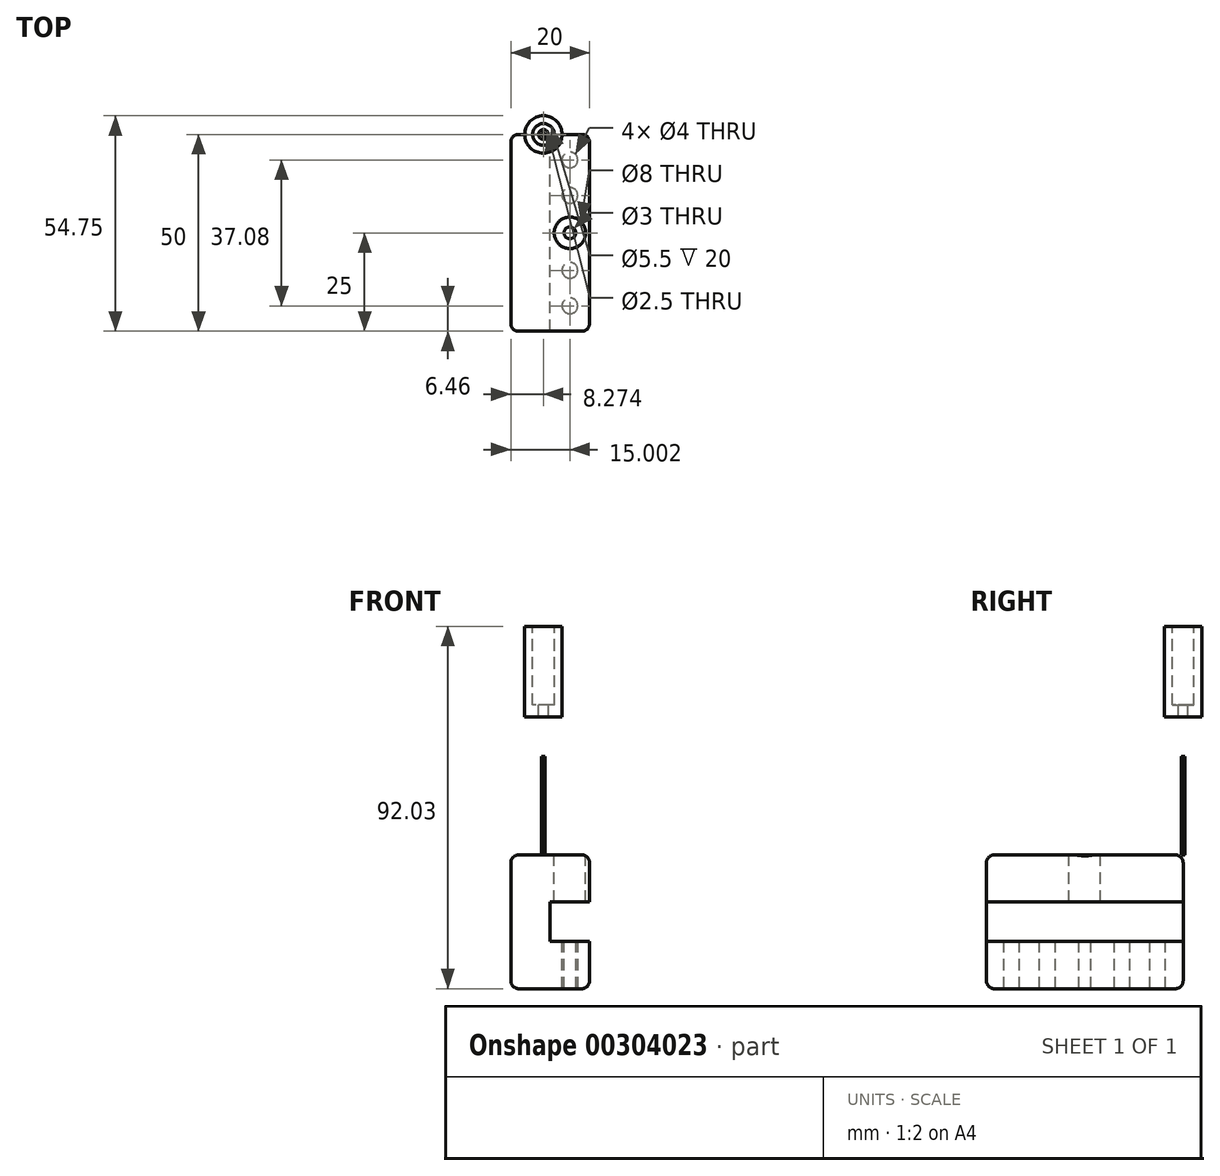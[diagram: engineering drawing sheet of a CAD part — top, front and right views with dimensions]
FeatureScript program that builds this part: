
annotation { "Feature Type Name" : "Feature", "Feature Type Description" : "" }
export const myFeature = defineFeature(function(context is Context, id is Id, definition is map)
    precondition{}
    {
        {
            var Q0;
            Q0=qCreatedBy(makeId("Front.planeOp"),FACE);
            var sketch = newSketch(context, id + "F0", { "sketchPlane" : qUnion([Q0])});
            skLineSegment(sketch, "E0", {"start": v(1.64, 12) * mm, "end": v(21.64, 12) * mm});
            skLineSegment(sketch, "E1", {"start": v(21.64, 12) * mm, "end": v(21.64, 0) * mm});
            skLineSegment(sketch, "E2", {"start": v(21.64, 0) * mm, "end": v(11.64, 0) * mm});
            skLineSegment(sketch, "E3", {"start": v(11.64, 0) * mm, "end": v(11.64, -10) * mm});
            skLineSegment(sketch, "E4", {"start": v(11.64, -10) * mm, "end": v(21.64, -10) * mm});
            skLineSegment(sketch, "E5", {"start": v(21.64, -10) * mm, "end": v(21.64, -22) * mm});
            skLineSegment(sketch, "E6", {"start": v(21.64, -22) * mm, "end": v(1.64, -22) * mm});
            skLineSegment(sketch, "E7", {"start": v(1.64, -22) * mm, "end": v(1.64, 12) * mm});
            skSolve(sketch);
        }
        {
            var Q0;
            Q0=makeQuery(id+"F0.imprint","IMPRINT",FACE,{"disambiguationData":[TD([[makeQuery(id+"F0.imprint","IMPRINT",EDGE,{"derivedFrom":sQuery(id+"F0.wireOp",EDGE,"E0")}),-1.0]])]});
            extrude(context, id + "F1", {"entities" : qUnion([Q0]), "depth" : 50 * mm});
        }
        {
            var Q0;
            Q0=makeQuery(id+"F1.opExtrude","SWEPT_FACE",FACE,{"disambiguationData":[OSD([sQuery(id+"F0.wireOp",EDGE,"E0")])]});
            var sketch = newSketch(context, id + "F2", { "sketchPlane" : qUnion([Q0])});
            skPoint(sketch, "E8", {"position": v(16.64, -25) * mm});
            skSolve(sketch);
        }
        {
            var Q0;
            Q0=sQuery(id+"F2.wireOp",VERTEX,"E8");
            var Q1;
            Q1=makeQuery(id+"F1.opExtrude","SWEPT_BODY",BODY,{"disambiguationData":[OSD([sQuery(id+"F0.wireOp",EDGE,"E0"),sQuery(id+"F0.wireOp",EDGE,"E1"),sQuery(id+"F0.wireOp",EDGE,"E2"),sQuery(id+"F0.wireOp",EDGE,"E3"),sQuery(id+"F0.wireOp",EDGE,"E4"),sQuery(id+"F0.wireOp",EDGE,"E5"),sQuery(id+"F0.wireOp",EDGE,"E6"),sQuery(id+"F0.wireOp",EDGE,"E7")])]});
            hole(context, id + "F3", {"style" : HoleStyle.SIMPLE, "endStyle" : HoleEndStyle.BLIND, "holeDiameter" : 8 * mm, "holeDepth" : 12 * mm, "tappedDepth" : 12 * mm, "tapClearance" : 3, "locations" : qUnion([Q0]), "scope" : qUnion([Q1])});
        }
        {
            var Q0;
            Q0=makeQuery(id+"F1.opExtrude","SWEPT_FACE",FACE,{"disambiguationData":[OSD([sQuery(id+"F0.wireOp",EDGE,"E4")])]});
            var sketch = newSketch(context, id + "F4", { "sketchPlane" : qUnion([Q0])});
            skPoint(sketch, "E9", {"position": v(16.64, -25) * mm});
            skSolve(sketch);
        }
        {
            var Q0;
            Q0=sQuery(id+"F4.wireOp",VERTEX,"E9");
            var Q1;
            Q1=makeQuery(id+"F1.opExtrude","SWEPT_BODY",BODY,{"disambiguationData":[OSD([sQuery(id+"F0.wireOp",EDGE,"E0"),sQuery(id+"F0.wireOp",EDGE,"E1"),sQuery(id+"F0.wireOp",EDGE,"E2"),sQuery(id+"F0.wireOp",EDGE,"E3"),sQuery(id+"F0.wireOp",EDGE,"E4"),sQuery(id+"F0.wireOp",EDGE,"E5"),sQuery(id+"F0.wireOp",EDGE,"E6"),sQuery(id+"F0.wireOp",EDGE,"E7")])]});
            hole(context, id + "F5", {"style" : HoleStyle.SIMPLE, "endStyle" : HoleEndStyle.THROUGH, "holeDiameter" : 3 * mm, "tappedDepth" : 12 * mm, "tapClearance" : 3, "locations" : qUnion([Q0]), "scope" : qUnion([Q1])});
        }
        {
            var Q0;
            Q0=makeQuery(id+"F1.opExtrude","SWEPT_FACE",FACE,{"disambiguationData":[OSD([sQuery(id+"F0.wireOp",EDGE,"E4")])]});
            var sketch = newSketch(context, id + "F6", { "sketchPlane" : qUnion([Q0])});
            skPoint(sketch, "E10", {"position": v(16.64, -34.52) * mm});
            skSolve(sketch);
        }
        {
            var Q0;
            Q0=sQuery(id+"F6.wireOp",VERTEX,"E10");
            var Q1;
            Q1=makeQuery(id+"F1.opExtrude","SWEPT_BODY",BODY,{"disambiguationData":[OSD([sQuery(id+"F0.wireOp",EDGE,"E0"),sQuery(id+"F0.wireOp",EDGE,"E1"),sQuery(id+"F0.wireOp",EDGE,"E2"),sQuery(id+"F0.wireOp",EDGE,"E3"),sQuery(id+"F0.wireOp",EDGE,"E4"),sQuery(id+"F0.wireOp",EDGE,"E5"),sQuery(id+"F0.wireOp",EDGE,"E6"),sQuery(id+"F0.wireOp",EDGE,"E7")])]});
            hole(context, id + "F7", {"style" : HoleStyle.SIMPLE, "endStyle" : HoleEndStyle.THROUGH, "holeDiameter" : 4 * mm, "tappedDepth" : 12 * mm, "tapClearance" : 3, "locations" : qUnion([Q0]), "scope" : qUnion([Q1])});
        }
        {
            var Q0;
            Q0=makeQuery(id+"F1.opExtrude","SWEPT_FACE",FACE,{"disambiguationData":[OSD([sQuery(id+"F0.wireOp",EDGE,"E4")])]});
            var sketch = newSketch(context, id + "F8", { "sketchPlane" : qUnion([Q0])});
            skPoint(sketch, "E11", {"position": v(16.64, -15.48) * mm});
            skSolve(sketch);
        }
        {
            var Q0;
            Q0=sQuery(id+"F8.wireOp",VERTEX,"E11");
            var Q1;
            Q1=makeQuery(id+"F1.opExtrude","SWEPT_BODY",BODY,{"disambiguationData":[OSD([sQuery(id+"F0.wireOp",EDGE,"E0"),sQuery(id+"F0.wireOp",EDGE,"E1"),sQuery(id+"F0.wireOp",EDGE,"E2"),sQuery(id+"F0.wireOp",EDGE,"E3"),sQuery(id+"F0.wireOp",EDGE,"E4"),sQuery(id+"F0.wireOp",EDGE,"E5"),sQuery(id+"F0.wireOp",EDGE,"E6"),sQuery(id+"F0.wireOp",EDGE,"E7")])]});
            hole(context, id + "F9", {"style" : HoleStyle.SIMPLE, "endStyle" : HoleEndStyle.THROUGH, "holeDiameter" : 4 * mm, "tappedDepth" : 12 * mm, "tapClearance" : 3, "locations" : qUnion([Q0]), "scope" : qUnion([Q1])});
        }
        {
            var Q0;
            Q0=makeQuery(id+"F1.opExtrude","SWEPT_FACE",FACE,{"disambiguationData":[OSD([sQuery(id+"F0.wireOp",EDGE,"E4")])]});
            var sketch = newSketch(context, id + "F10", { "sketchPlane" : qUnion([Q0])});
            skPoint(sketch, "E12", {"position": v(16.64, -6.46) * mm});
            skSolve(sketch);
        }
        {
            var Q0;
            Q0=sQuery(id+"F10.wireOp",VERTEX,"E12");
            var Q1;
            Q1=makeQuery(id+"F1.opExtrude","SWEPT_BODY",BODY,{"disambiguationData":[OSD([sQuery(id+"F0.wireOp",EDGE,"E0"),sQuery(id+"F0.wireOp",EDGE,"E1"),sQuery(id+"F0.wireOp",EDGE,"E2"),sQuery(id+"F0.wireOp",EDGE,"E3"),sQuery(id+"F0.wireOp",EDGE,"E4"),sQuery(id+"F0.wireOp",EDGE,"E5"),sQuery(id+"F0.wireOp",EDGE,"E6"),sQuery(id+"F0.wireOp",EDGE,"E7")])]});
            hole(context, id + "F11", {"style" : HoleStyle.SIMPLE, "endStyle" : HoleEndStyle.THROUGH, "holeDiameter" : 4 * mm, "tappedDepth" : 12 * mm, "tapClearance" : 3, "locations" : qUnion([Q0]), "scope" : qUnion([Q1])});
        }
        {
            var Q0;
            Q0=makeQuery(id+"F1.opExtrude","SWEPT_FACE",FACE,{"disambiguationData":[OSD([sQuery(id+"F0.wireOp",EDGE,"E4")])]});
            var sketch = newSketch(context, id + "F12", { "sketchPlane" : qUnion([Q0])});
            skPoint(sketch, "E13", {"position": v(16.64, -43.54) * mm});
            skSolve(sketch);
        }
        {
            var Q0;
            Q0=sQuery(id+"F12.wireOp",VERTEX,"E13");
            var Q1;
            Q1=makeQuery(id+"F1.opExtrude","SWEPT_BODY",BODY,{"disambiguationData":[OSD([sQuery(id+"F0.wireOp",EDGE,"E0"),sQuery(id+"F0.wireOp",EDGE,"E1"),sQuery(id+"F0.wireOp",EDGE,"E2"),sQuery(id+"F0.wireOp",EDGE,"E3"),sQuery(id+"F0.wireOp",EDGE,"E4"),sQuery(id+"F0.wireOp",EDGE,"E5"),sQuery(id+"F0.wireOp",EDGE,"E6"),sQuery(id+"F0.wireOp",EDGE,"E7")])]});
            hole(context, id + "F13", {"style" : HoleStyle.SIMPLE, "endStyle" : HoleEndStyle.THROUGH, "holeDiameter" : 4 * mm, "tappedDepth" : 12 * mm, "tapClearance" : 3, "locations" : qUnion([Q0]), "scope" : qUnion([Q1])});
        }
        {
            var Q0;
            Q0=makeQuery(id+"F1.opExtrude","SWEPT_EDGE",EDGE,{"disambiguationData":[OSD([sQuery(id+"F0.wireOp",EDGE,"E0"),sQuery(id+"F0.wireOp",EDGE,"E1")])]});
            fillet(context, id + "F14", {"entities" : qUnion([Q0]), "radius" : 2 * mm, "tangentPropagation" : true, "allowEdgeOverflow" : false});
        }
        {
            var Q0;
            Q0=makeQuery(id+"F1.opExtrude","SWEPT_EDGE",EDGE,{"disambiguationData":[OSD([sQuery(id+"F0.wireOp",EDGE,"E5"),sQuery(id+"F0.wireOp",EDGE,"E6")])]});
            fillet(context, id + "F15", {"entities" : qUnion([Q0]), "radius" : 2 * mm, "tangentPropagation" : true, "allowEdgeOverflow" : false});
        }
        {
            var Q0;
            Q0=makeQuery(id+"F1.opExtrude","SWEPT_EDGE",EDGE,{"disambiguationData":[OSD([sQuery(id+"F0.wireOp",EDGE,"E0"),sQuery(id+"F0.wireOp",EDGE,"E7")])]});
            var Q1;
            Q1=makeQuery(id+"F1.opExtrude","SWEPT_EDGE",EDGE,{"disambiguationData":[OSD([sQuery(id+"F0.wireOp",EDGE,"E6"),sQuery(id+"F0.wireOp",EDGE,"E7")])]});
            fillet(context, id + "F16", {"entities" : qUnion([Q0, Q1]), "radius" : 2 * mm, "tangentPropagation" : true, "allowEdgeOverflow" : false});
        }
        {
            var Q0;
            Q0=makeQuery(id+"F1.opExtrude","CAP_EDGE",EDGE,{"disambiguationData":[OSD([sQuery(id+"F0.wireOp",EDGE,"E6")])],"isStart":false});
            var Q1;
            Q1=makeQuery(id+"F1.opExtrude","CAP_EDGE",EDGE,{"disambiguationData":[OSD([sQuery(id+"F0.wireOp",EDGE,"E7")])],"isStart":false});
            var Q2;
            Q2=makeQuery(id+"F1.opExtrude","CAP_EDGE",EDGE,{"disambiguationData":[OSD([sQuery(id+"F0.wireOp",EDGE,"E0")])],"isStart":false});
            var Q3;
            Q3=makeQuery(id+"F1.opExtrude","CAP_EDGE",EDGE,{"disambiguationData":[OSD([sQuery(id+"F0.wireOp",EDGE,"E0")])],"isStart":true});
            var Q4;
            Q4=makeQuery(id+"F1.opExtrude","CAP_EDGE",EDGE,{"disambiguationData":[OSD([sQuery(id+"F0.wireOp",EDGE,"E7")])],"isStart":true});
            fillet(context, id + "F17", {"entities" : qUnion([Q0, Q1, Q2, Q3, Q4]), "radius" : 2 * mm, "tangentPropagation" : true, "allowEdgeOverflow" : false});
        }
        {
            var Q0;
            Q0=qCreatedBy(makeId("Front.planeOp"),FACE);
            var sketch = newSketch(context, id + "F18", { "sketchPlane" : qUnion([Q0])});
            skLineSegment(sketch, "E14", {"start": v(14.66, 47.03) * mm, "end": v(14.66, 70.03) * mm});
            skLineSegment(sketch, "E15", {"start": v(14.66, 70.03) * mm, "end": v(12.66, 70.03) * mm});
            skLineSegment(sketch, "E16", {"start": v(12.66, 70.03) * mm, "end": v(12.66, 50.03) * mm});
            skLineSegment(sketch, "E17", {"start": v(12.66, 50.03) * mm, "end": v(11.16, 50.03) * mm});
            skLineSegment(sketch, "E18", {"start": v(11.16, 50.03) * mm, "end": v(11.16, 47.03) * mm});
            skLineSegment(sketch, "E19", {"start": v(11.16, 47.03) * mm, "end": v(14.66, 47.03) * mm});
            skSolve(sketch);
        }
        {
            var Q0;
            Q0=qCreatedBy(makeId("Front.planeOp"),FACE);
            var sketch = newSketch(context, id + "F19", { "sketchPlane" : qUnion([Q0])});
            skPoint(sketch, "E20", {"position": v(9.91, 47.56) * mm});
            skSolve(sketch);
        }
        {
            var Q0;
            Q0=makeQuery(id+"F1.opExtrude","SWEPT_FACE",FACE,{"disambiguationData":[OSD([sQuery(id+"F0.wireOp",EDGE,"E0")])]});
            var sketch = newSketch(context, id + "F20", { "sketchPlane" : qUnion([Q0])});
            skCircle(sketch, "E21", {"center": v(9.91, 0) * mm, "radius": 0.43 * mm});
            skSolve(sketch);
        }
        {
            var Q0;
            Q0=makeQuery(id+"F20.imprint","IMPRINT",FACE,{"disambiguationData":[TD([[makeQuery(id+"F20.imprint","IMPRINT",EDGE,{"derivedFrom":sQuery(id+"F20.wireOp",EDGE,"E21")}),1.0]])]});
            extrude(context, id + "F21", {"entities" : qUnion([Q0]), "depth" : 25 * mm});
        }
        {
            var Q0;
            Q0=makeQuery(id+"F18.imprint","IMPRINT",FACE,{"disambiguationData":[TD([[makeQuery(id+"F18.imprint","IMPRINT",EDGE,{"derivedFrom":sQuery(id+"F18.wireOp",EDGE,"E14")}),1.0]])]});
            var Q1;
            Q1=makeQuery(id+"F21.opExtrude","SWEPT_FACE",FACE,{"disambiguationData":[OSD([sQuery(id+"F20.wireOp",EDGE,"E21")])]});
            revolve(context, id + "F22", {"entities" : qUnion([Q0]), "axis" : qUnion([Q1]), "revolveType" : RevolveType.FULL});
        }
    });
